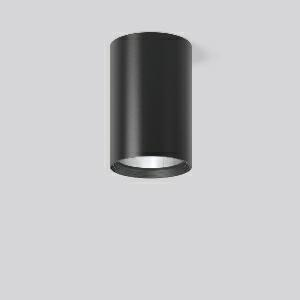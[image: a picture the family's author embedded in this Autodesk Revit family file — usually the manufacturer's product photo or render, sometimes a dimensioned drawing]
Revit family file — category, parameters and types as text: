
# Revit family: heledon_maxi_a_931233_003_2dc4
name_source: partatom
category: Lighting Fixtures
units: mm (PartAtom-declared; Revit-internal decimal feet)

## family parameters
Cut with Voids When Loaded = No
Host = Face
Light Source = No
Part Type = Normal
Room Calculation Point = No
Round Connector Dimension = Use Diameter
Shared = No

## types (1)
- HELEDON maxi A (1 x LED Modul 932 fresh meat, 2050 lm, 3200)
    Apparent Load = 33 VA
    Approval mark = CE
    CIE Flux Codes = 96 100 100 100 100
    Color Rendering = 90
    Color Temperature = 3200
    Default Elevation = 1800 mm
    Description = Series: HELEDON maxi
Cylindrical surface-mounted downlight. Housing: die-cast aluminium, powder-coated. Internal ceiling frame polycarbonate with bayonet mounting. Black plastic ring and recessed LED to prevent glare from the side. Optical assembly with reflector made of MIRO-Silver with 98% total light reflection for outstanding efficiency - can be changed without tools. Special LED for illumination of meat included. Suitable for Ceiling mounting. Easy installation with a separate ceiling frame with bayonet mounting and plug connection. Driver integrated. Connected via plug-in connector. High quality converter without flickering and stroboscopic effect. The following accessories can be mounted without use of tools: interchangeable lenses, decorative glasses, honeycomb louvre, clear and frosted diffusers, white interchangeable plastic ring. 
Colour: deep black, matt (RAL 9005)
Diameter: 123 mm
Height: 183 mm
Lamp: LED
Socket: without socket
Colour temperature: fresh meat
System power: 33 W
Rated luminous flux: 2050 lm
Luminous efficiency: 62 lm/W
Control gear: Regulated power supply
Protection class: I
Type of protection: IP 20
    Height = 183 mm
    Lamp = 1 x LED Modul 932 fresh meat
    Lamp Light Flux = 2050 lm
    Lamp count = 1
    Length = 123 mm
    Lifetime = 50000 h
    Luminous efficacy = 62 lm/W
    Manufacturer = RZB
    ModVariant = No
    Model = 931233.003
    Mounting Place = Ceiling
    Mounting Type = Surface mounted
    Number of Poles = 1
    OnlyDefault = Yes
    Power Factor = 1
    Product Name = HELEDON maxi A
    Product group = Surface mounted downlights
    ProductGroupID = 302
    Protection Class = Protection class I
    Protection Degree = IP 20
    RLX_Detail_Level = 1
    RLX_Emergency_Light_Flux = 0 lm
    RLX_Emergency_Type = 0
    RLX_Emergency_Type_DB = No
    RlxData = <blob elided: 98217 chars, md5=007f53d7>
    Socket = socket
    Standby Power = 0 W
    System Light Flux = 2050 lm
    System Power = 33 W
    Type Comments = Product without accessories
    Type Image = 931192.003.jpg
    URL = http://relux.com
    VarID = ---
    Voltage = 230 V
    Voltage Range = 220-240 V
    Weight = 0.00 kg
    Width = 0 mm  [stored 0 ft]

note: [stored X ft] marks values corroborated as IEEE doubles in the binary element streams (Revit-internal decimal feet)

## geometry (parser evidence)
native form markers: Blend x4, Sweep x10
no freeform markers — native parametric forms only
